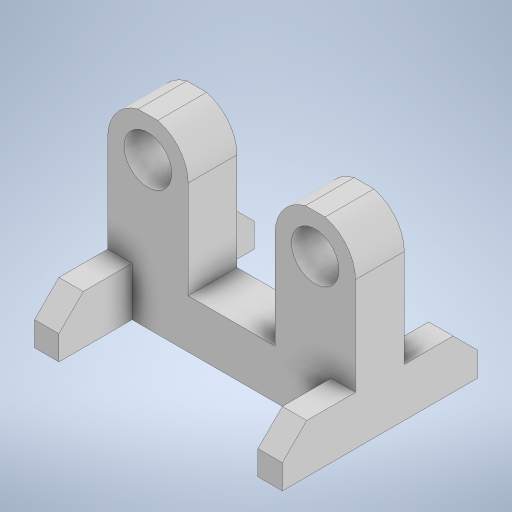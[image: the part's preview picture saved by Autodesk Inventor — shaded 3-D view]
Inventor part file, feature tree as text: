
AUTODESK INVENTOR PART (.ipt)
format: ipt  version: 2024 (Build 280153000, 153)  size: 282,112 bytes
history: native  units: mm
features: extrude x2, sketch x2, plane x1, chamfer x1, projected_geometry x1
ambient origin geometry x8: Origin, YZ Plane, XZ Plane, XY Plane, X Axis, Y Axis, Z Axis, Center Point
bodies: Solid1 (feature_tree)
feature tree (7):
  extrude  "Extrusion1"  Depth=50.8mm
  plane  "Work Plane1"
  extrude  "Extrusion2"  Depth=28.0mm
  chamfer  "Chamfer1"  Distance=16.5mm
  sketch  "Sketch1"  dims[d0=0.0mm d1=50.8mm]
  sketch  "Sketch2"  dims[d2=8.25mm d3=9.75mm d4=16.5mm d5=10.0mm d6=0.0mm d7=10.0mm d8=0.0mm d9=-5.0mm d10=5.0mm d11=5.0mm d12=10.0mm d13=10.0mm d14=40.0mm d15=0.0mm d16=5.0mm d17=2.0mm d18=45.0deg d19=20.0mm d21=28.0mm]
  projected_geometry  "Projected Loop1"
